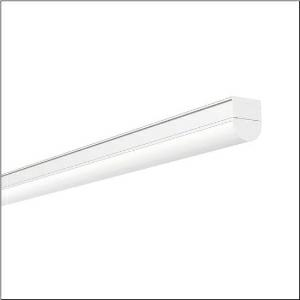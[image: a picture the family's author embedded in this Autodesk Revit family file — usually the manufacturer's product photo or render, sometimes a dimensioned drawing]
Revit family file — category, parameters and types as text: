
# Revit family: ecopack_r__31_51lj12mkm40a_d749
name_source: partatom
category: Lighting Fixtures
units: mm (PartAtom-declared; Revit-internal decimal feet)

## family parameters
Cut with Voids When Loaded = No
Host = Face
Light Source = No
Part Type = Normal
Room Calculation Point = No
Round Connector Dimension = Use Diameter
Shared = No

## types (1)
- --- (1 x LED, 4890 lm, 35 W, 5000K)
    Apparent Load = 35 VA
    CIE Flux Codes = 39 67 87 89 100
    Color Rendering = 80
    Color Temperature = 5000K
    Default Elevation = 1800 mm
    Description = Ecopack® 31, diffuser luminaire, primary optical cover: cover, of PC, frosted, light emission: direct distribution, primary light characteristic: symmetric, installation type: surface-mounted, LED, rated luminous flux: 4.800lm, luminous efficacy: 135lm/W, light colour: 830/840/850, colour temperature: 3000/4000/5000K, control gear: ECG, with terminal, 3-pole, mains connection: 220..240V, AC, 50/60Hz, rated input power: 35W, housing, of aluminium, traffic white (RAL 9016), length: 1.149mm, width: 56mm, height: 68mm, end cap, of PC, white, protection rating (complete): IP20, insulation class (complete): insulation class I (protective earthing), certification: CE, impact resistance: IK06, permissible operating ambient temperature: -20..+40°C, packaging unit: 1 piece
    Height = 68 mm
    Lamp = 1 x LED
    Lamp Light Flux = 4890 lm
    Lamp Power = 35 W
    Lamp count = 1
    Length = 1149 mm
    Luminous efficacy = 140 lm/W
    Manufacturer = Siteco
    ModVariant = No
    Model = 51LJ12MKM40A
    Mounting Place = Ceiling
    Mounting Type = Surface mounted
    Number of Poles = 1
    OnlyDefault = Yes
    Power Factor = 1
    Product Name = Ecopack® 31
    Product group = diffuser luminaire
    ProductGroupID = 303
    Protection Class = Protection class I
    Protection Degree = IP 20
    RLX_Detail_Level = 1
    RlxData = <blob elided: 42421 chars, md5=79966a15>
    Socket = socket
    Standby Power = 0 W
    System Light Flux = 4890 lm
    System Power = 35 W
    Type Comments = individual setting: colour temperature 5000K, luminous flux: 100 % | (ON | ON)
    Type Image = l_1007030.jpg
    URL = http://relux.com
    VarID = @adj_086355
    Voltage = 0 V
    Weight = 0.00 kg
    Width = 56 mm

## geometry (parser evidence)
native form markers: Blend x4, Sweep x12
no freeform markers — native parametric forms only
